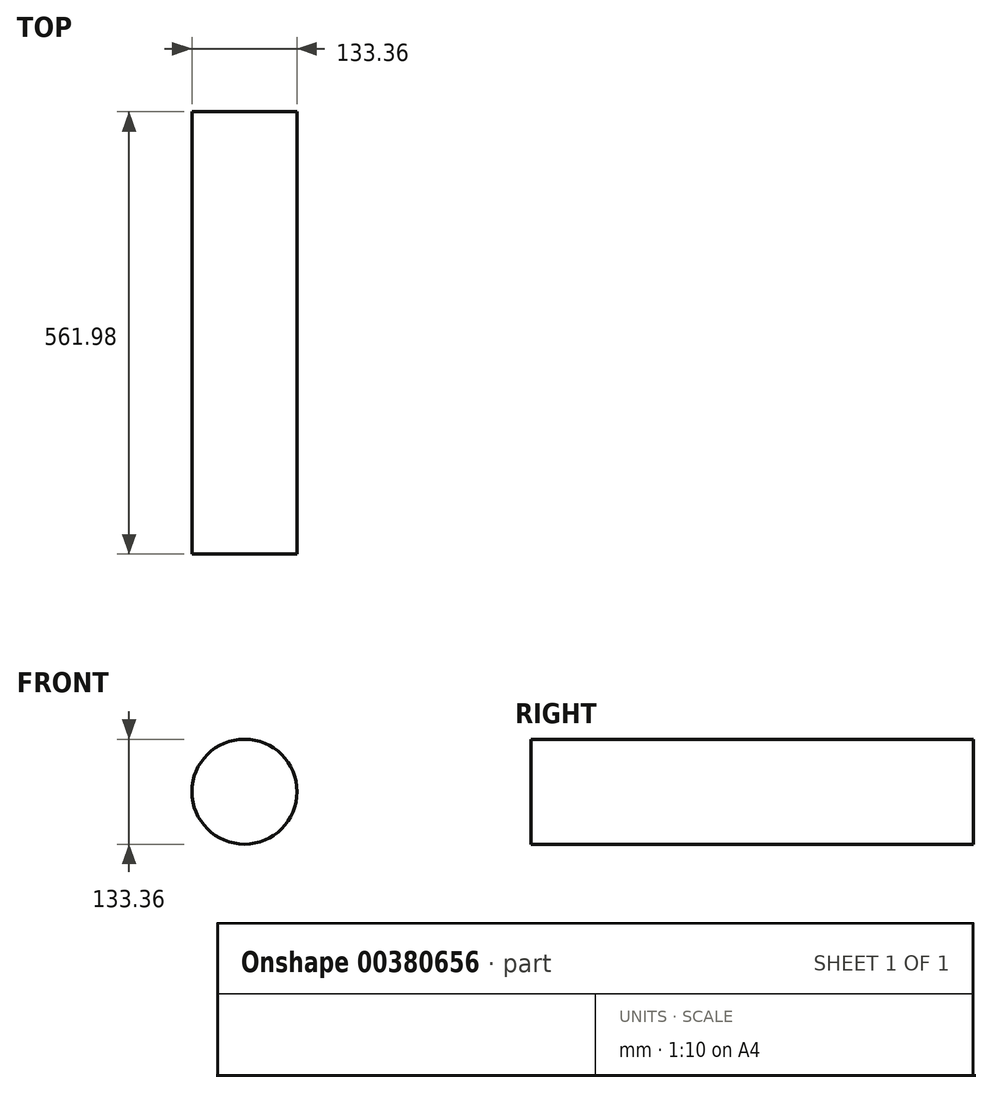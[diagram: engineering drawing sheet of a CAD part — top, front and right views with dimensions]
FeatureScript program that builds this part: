
annotation { "Feature Type Name" : "Feature", "Feature Type Description" : "" }
export const myFeature = defineFeature(function(context is Context, id is Id, definition is map)
    precondition{}
    {
        {
            var Q0;
            Q0=qCreatedBy(makeId("Front.planeOp"),FACE);
            var sketch = newSketch(context, id + "F0", { "sketchPlane" : qUnion([Q0])});
            skCircle(sketch, "E0", {"center": v(0, 0) * mm, "radius": 66.67 * mm});
            skSolve(sketch);
        }
        {
            var Q0;
            Q0=makeQuery(id+"F0.imprint","IMPRINT",FACE,{"disambiguationData":[TD([[makeQuery(id+"F0.imprint","IMPRINT",EDGE,{"derivedFrom":sQuery(id+"F0.wireOp",EDGE,"E0")}),1.0]])]});
            extrude(context, id + "F1", {"entities" : qUnion([Q0]), "depth" : 561.98 * mm});
        }
    });
